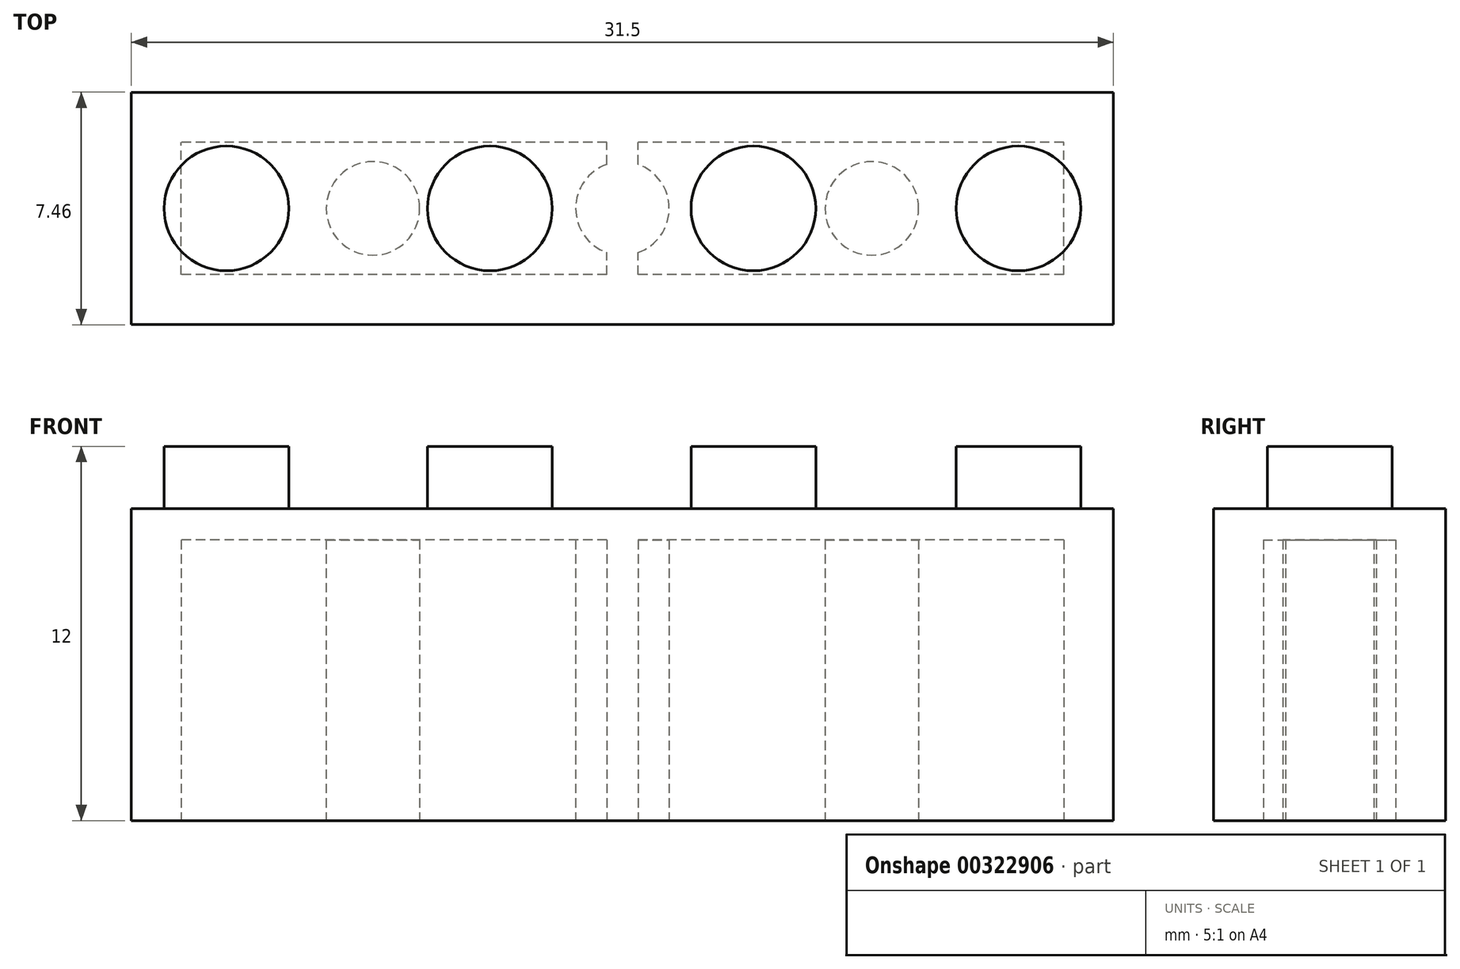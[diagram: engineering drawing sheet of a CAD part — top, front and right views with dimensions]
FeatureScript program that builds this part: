
annotation { "Feature Type Name" : "Feature", "Feature Type Description" : "" }
export const myFeature = defineFeature(function(context is Context, id is Id, definition is map)
    precondition{}
    {
        {
            var Q0;
            Q0=qCreatedBy(makeId("Top.planeOp"),FACE);
            var sketch = newSketch(context, id + "F0", { "sketchPlane" : qUnion([Q0])});
            skLineSegment(sketch, "E0.bottom", {"start": v(15.75, 3.73) * mm, "end": v(-15.75, 3.73) * mm});
            skLineSegment(sketch, "E0.top", {"start": v(15.75, -3.73) * mm, "end": v(-15.75, -3.73) * mm});
            skLineSegment(sketch, "E0.left", {"start": v(15.75, 3.73) * mm, "end": v(15.75, -3.73) * mm});
            skLineSegment(sketch, "E0.right", {"start": v(-15.75, 3.73) * mm, "end": v(-15.75, -3.73) * mm});
            skPoint(sketch, "E0.middle", {"position": v(0, 0) * mm});
            skCircle(sketch, "E1", {"center": v(-12.7, 0) * mm, "radius": 2 * mm});
            skCircle(sketch, "E2", {"center": v(12.7, 0) * mm, "radius": 2 * mm});
            skCircle(sketch, "E3", {"center": v(-4.25, 0) * mm, "radius": 2 * mm});
            skCircle(sketch, "E4", {"center": v(4.2, 0) * mm, "radius": 2 * mm});
            skSolve(sketch);
        }
        {
            var Q0;
            Q0=makeQuery(id+"F0.imprint","IMPRINT",FACE,{"disambiguationData":[TD([[makeQuery(id+"F0.imprint","IMPRINT",EDGE,{"derivedFrom":sQuery(id+"F0.wireOp",EDGE,"E0.bottom")}),1.0]])]});
            extrude(context, id + "F1", {"entities" : qUnion([Q0]), "depth" : 10 * mm});
        }
        {
            var Q0;
            Q0=makeQuery(id+"F0.imprint","IMPRINT",FACE,{"disambiguationData":[TD([[makeQuery(id+"F0.imprint","IMPRINT",EDGE,{"derivedFrom":sQuery(id+"F0.wireOp",EDGE,"E1")}),1.0]])]});
            var Q1;
            Q1=makeQuery(id+"F0.imprint","IMPRINT",FACE,{"disambiguationData":[TD([[makeQuery(id+"F0.imprint","IMPRINT",EDGE,{"derivedFrom":sQuery(id+"F0.wireOp",EDGE,"E3")}),1.0]])]});
            var Q2;
            Q2=makeQuery(id+"F0.imprint","IMPRINT",FACE,{"disambiguationData":[TD([[makeQuery(id+"F0.imprint","IMPRINT",EDGE,{"derivedFrom":sQuery(id+"F0.wireOp",EDGE,"E4")}),1.0]])]});
            var Q3;
            Q3=makeQuery(id+"F0.imprint","IMPRINT",FACE,{"disambiguationData":[TD([[makeQuery(id+"F0.imprint","IMPRINT",EDGE,{"derivedFrom":sQuery(id+"F0.wireOp",EDGE,"E2")}),1.0]])]});
            extrude(context, id + "F2", {"entities" : qUnion([Q0, Q1, Q2, Q3]), "operationType" : NewBodyOperationType.ADD, "depth" : 12 * mm});
        }
        {
            var Q0;
            {var subQ0=sQuery(id+"F0.wireOp",EDGE,"E4");var subQ1=sQuery(id+"F0.wireOp",EDGE,"E3");var subQ2=sQuery(id+"F0.wireOp",EDGE,"E2");var subQ3=sQuery(id+"F0.wireOp",EDGE,"E1");Q0=makeQuery(id+"F2.boolean.opBoolean","MERGE",FACE,{"derivedFrom":[makeQuery(id+"F1.opExtrude","CAP_FACE",FACE,{"disambiguationData":[OSD([sQuery(id+"F0.wireOp",EDGE,"E0.bottom"),sQuery(id+"F0.wireOp",EDGE,"E0.top"),sQuery(id+"F0.wireOp",EDGE,"E0.left"),sQuery(id+"F0.wireOp",EDGE,"E0.right"),subQ3,subQ2,subQ1,subQ0])],"isStart":true}),makeQuery(id+"F2.opExtrude","CAP_FACE",FACE,{"disambiguationData":[OSD([subQ3])],"isStart":true}),makeQuery(id+"F2.opExtrude","CAP_FACE",FACE,{"disambiguationData":[OSD([subQ2])],"isStart":true}),makeQuery(id+"F2.opExtrude","CAP_FACE",FACE,{"disambiguationData":[OSD([subQ1])],"isStart":true}),makeQuery(id+"F2.opExtrude","CAP_FACE",FACE,{"disambiguationData":[OSD([subQ0])],"isStart":true})]});}
            var sketch = newSketch(context, id + "F3", { "sketchPlane" : qUnion([Q0])});
            skLineSegment(sketch, "E5.bottom", {"start": v(14.15, 2.13) * mm, "end": v(-14.15, 2.13) * mm});
            skLineSegment(sketch, "E5.top", {"start": v(14.15, -2.13) * mm, "end": v(-14.15, -2.13) * mm});
            skLineSegment(sketch, "E5.left", {"start": v(14.15, 2.13) * mm, "end": v(14.15, -2.13) * mm});
            skLineSegment(sketch, "E5.right", {"start": v(-14.15, 2.13) * mm, "end": v(-14.15, -2.13) * mm});
            skPoint(sketch, "E5.middle", {"position": v(0, 0) * mm});
            skCircle(sketch, "E6", {"center": v(0, 0) * mm, "radius": 1.5 * mm});
            skCircle(sketch, "E7", {"center": v(8, 0) * mm, "radius": 1.5 * mm});
            skCircle(sketch, "E8", {"center": v(-8, 0) * mm, "radius": 1.5 * mm});
            skLineSegment(sketch, "E9.bottom", {"start": v(0.5, 2.13) * mm, "end": v(-0.5, 2.13) * mm});
            skLineSegment(sketch, "E9.top", {"start": v(0.5, -2.13) * mm, "end": v(-0.5, -2.13) * mm});
            skLineSegment(sketch, "E9.left", {"start": v(0.5, 2.13) * mm, "end": v(0.5, -2.13) * mm});
            skLineSegment(sketch, "E9.right", {"start": v(-0.5, 2.13) * mm, "end": v(-0.5, -2.13) * mm});
            skSolve(sketch);
        }
        {
            var Q0;
            {var subQ4=sQuery(id+"F3.wireOp",EDGE,"E5.left");Q0=makeQuery(id+"F3.imprint","IMPRINT",FACE,{"disambiguationData":[TD([[makeQuery(id+"F3.imprint","IMPRINT",EDGE,{"derivedFrom":subQ4}),-1.0]])]});}
            var Q1;
            {var subQ4=sQuery(id+"F3.wireOp",EDGE,"E5.right");Q1=makeQuery(id+"F3.imprint","IMPRINT",FACE,{"disambiguationData":[TD([[makeQuery(id+"F3.imprint","IMPRINT",EDGE,{"derivedFrom":subQ4}),1.0]])]});}
            extrude(context, id + "F4", {"entities" : qUnion([Q0, Q1]), "operationType" : NewBodyOperationType.REMOVE, "oppositeDirection" : true, "depth" : 9 * mm});
        }
    });
